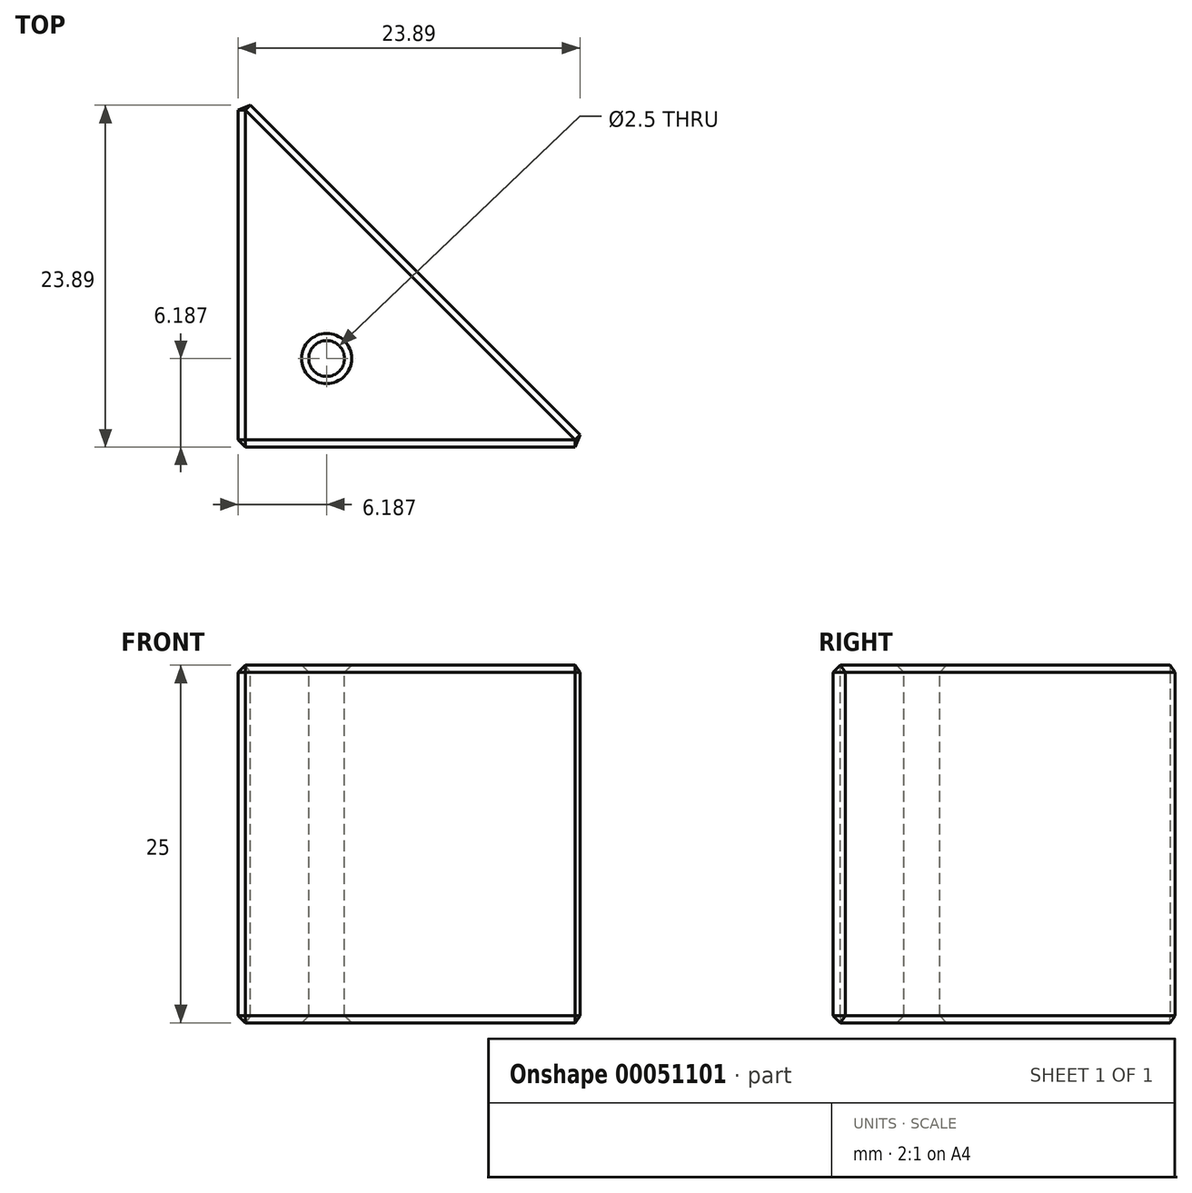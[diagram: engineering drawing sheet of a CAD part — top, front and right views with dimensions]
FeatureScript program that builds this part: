
annotation { "Feature Type Name" : "Feature", "Feature Type Description" : "" }
export const myFeature = defineFeature(function(context is Context, id is Id, definition is map)
    precondition{}
    {
        {
            var Q0;
            Q0=qCreatedBy(makeId("Top.planeOp"),FACE);
            var sketch = newSketch(context, id + "F0", { "sketchPlane" : qUnion([Q0])});
            skLineSegment(sketch, "E0.bottom", {"start": v(0, 0) * mm, "end": v(24.75, 0) * mm});
            skLineSegment(sketch, "E0.top", {"start": v(0, 24.75) * mm, "end": v(24.75, 24.75) * mm});
            skLineSegment(sketch, "E0.left", {"start": v(0, 0) * mm, "end": v(0, 24.75) * mm});
            skLineSegment(sketch, "E0.right", {"start": v(24.75, 0) * mm, "end": v(24.75, 24.75) * mm});
            skSolve(sketch);
        }
        {
            var Q0;
            Q0=makeQuery(id+"F0.imprint","IMPRINT",FACE,{"disambiguationData":[TD([[makeQuery(id+"F0.imprint","IMPRINT",EDGE,{"derivedFrom":sQuery(id+"F0.wireOp",EDGE,"E0.bottom")}),1.0]])]});
            extrude(context, id + "F1", {"entities" : qUnion([Q0]), "depth" : 25 * mm});
        }
        {
            var Q0;
            Q0=makeQuery(id+"F1.opExtrude","CAP_FACE",FACE,{"disambiguationData":[OSD([sQuery(id+"F0.wireOp",EDGE,"E0.bottom"),sQuery(id+"F0.wireOp",EDGE,"E0.top"),sQuery(id+"F0.wireOp",EDGE,"E0.left"),sQuery(id+"F0.wireOp",EDGE,"E0.right")])],"isStart":false});
            var sketch = newSketch(context, id + "F2", { "sketchPlane" : qUnion([Q0])});
            skLineSegment(sketch, "E1", {"start": v(0, 24.75) * mm, "end": v(0, 0) * mm});
            skLineSegment(sketch, "E2", {"start": v(0, 0) * mm, "end": v(24.75, 0) * mm});
            skLineSegment(sketch, "E3", {"start": v(24.75, 0) * mm, "end": v(0, 24.75) * mm});
            skSolve(sketch);
        }
        {
            var Q0;
            Q0=makeQuery(id+"F2.imprint","IMPRINT",FACE,{"disambiguationData":[TD([[makeQuery(id+"F2.imprint","IMPRINT",EDGE,{"derivedFrom":sQuery(id+"F2.wireOp",EDGE,"E3")}),-1.0]])]});
            extrude(context, id + "F3", {"entities" : qUnion([Q0]), "operationType" : NewBodyOperationType.REMOVE, "oppositeDirection" : true, "depth" : 25 * mm});
        }
        {
            var Q0;
            Q0=makeQuery(id+"F1.opExtrude","CAP_FACE",FACE,{"disambiguationData":[OSD([sQuery(id+"F0.wireOp",EDGE,"E0.bottom"),sQuery(id+"F0.wireOp",EDGE,"E0.top"),sQuery(id+"F0.wireOp",EDGE,"E0.left"),sQuery(id+"F0.wireOp",EDGE,"E0.right")])],"isStart":false});
            var sketch = newSketch(context, id + "F4", { "sketchPlane" : qUnion([Q0])});
            skCircle(sketch, "E4", {"center": v(6.19, 6.19) * mm, "radius": 1.25 * mm});
            skSolve(sketch);
        }
        {
            var Q0;
            Q0 = qSketchRegion(id + "F4", true);
            extrude(context, id + "F5", {"entities" : qUnion([Q0]), "operationType" : NewBodyOperationType.REMOVE, "oppositeDirection" : true, "depth" : 25 * mm});
        }
        {
            var Q0;
            Q0=makeQuery(id+"F3.boolean.opBoolean","COPY",FACE,{"derivedFrom":makeQuery(id+"F3.opExtrude","SWEPT_FACE",FACE,{"disambiguationData":[OSD([sQuery(id+"F2.wireOp",EDGE,"E3")])]})});
            var Q1;
            Q1=makeQuery(id+"F1.opExtrude","CAP_FACE",FACE,{"disambiguationData":[OSD([sQuery(id+"F0.wireOp",EDGE,"E0.bottom"),sQuery(id+"F0.wireOp",EDGE,"E0.top"),sQuery(id+"F0.wireOp",EDGE,"E0.left"),sQuery(id+"F0.wireOp",EDGE,"E0.right")])],"isStart":false});
            var Q2;
            Q2=makeQuery(id+"F1.opExtrude","SWEPT_FACE",FACE,{"disambiguationData":[OSD([sQuery(id+"F0.wireOp",EDGE,"E0.left")])]});
            var Q3;
            Q3=makeQuery(id+"F1.opExtrude","CAP_FACE",FACE,{"disambiguationData":[OSD([sQuery(id+"F0.wireOp",EDGE,"E0.bottom"),sQuery(id+"F0.wireOp",EDGE,"E0.top"),sQuery(id+"F0.wireOp",EDGE,"E0.left"),sQuery(id+"F0.wireOp",EDGE,"E0.right")])],"isStart":true});
            chamfer(context, id + "F6", {"entities" : qUnion([Q0, Q1, Q2, Q3]), "width" : 0.5 * mm, "tangentPropagation" : true});
        }
    });
